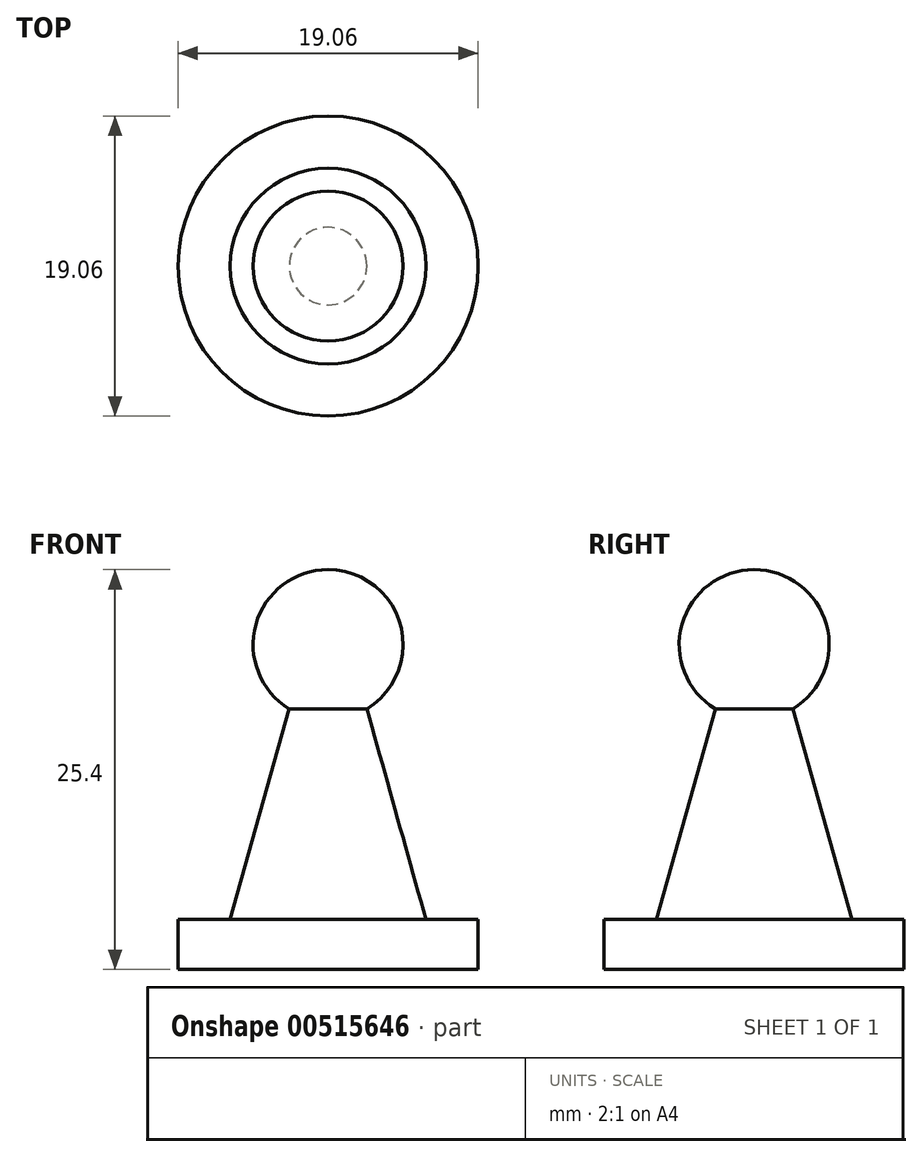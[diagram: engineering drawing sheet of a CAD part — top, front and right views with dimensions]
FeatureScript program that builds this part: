
annotation { "Feature Type Name" : "Feature", "Feature Type Description" : "" }
export const myFeature = defineFeature(function(context is Context, id is Id, definition is map)
    precondition{}
    {
        {
            var Q0;
            Q0=qCreatedBy(makeId("Front.planeOp"),FACE);
            var sketch = newSketch(context, id + "F0", { "sketchPlane" : qUnion([Q0])});
            skLineSegment(sketch, "E0.bottom", {"start": v(0, 0) * mm, "end": v(-9.53, 0) * mm});
            skLineSegment(sketch, "E0.top", {"start": v(-6.21, 3.18) * mm, "end": v(-9.53, 3.18) * mm});
            skLineSegment(sketch, "E0.left", {"start": v(0, 0) * mm, "end": v(0, 3.18) * mm});
            skLineSegment(sketch, "E0.right", {"start": v(-9.53, 0) * mm, "end": v(-9.53, 3.17) * mm});
            skArc(sketch, "E1", {"start": v(0, 25.4) * mm, "mid": v(-4.59, 21.92) * mm, "end": v(-2.46, 16.56) * mm});
            skLineSegment(sketch, "E2", {"start": v(-2.46, 16.56) * mm, "end": v(-6.21, 3.17) * mm});
            skLineSegment(sketch, "E3", {"start": v(0, 25.4) * mm, "end": v(0, 3.18) * mm});
            skSolve(sketch);
        }
        {
            var Q0;
            Q0 = qSketchRegion(id + "F0", true);
            var Q1;
            Q1=sQuery(id+"F0.wireOp",EDGE,"E3");
            revolve(context, id + "F1", {"entities" : qUnion([Q0]), "axis" : qUnion([Q1]), "revolveType" : RevolveType.FULL});
        }
    });
